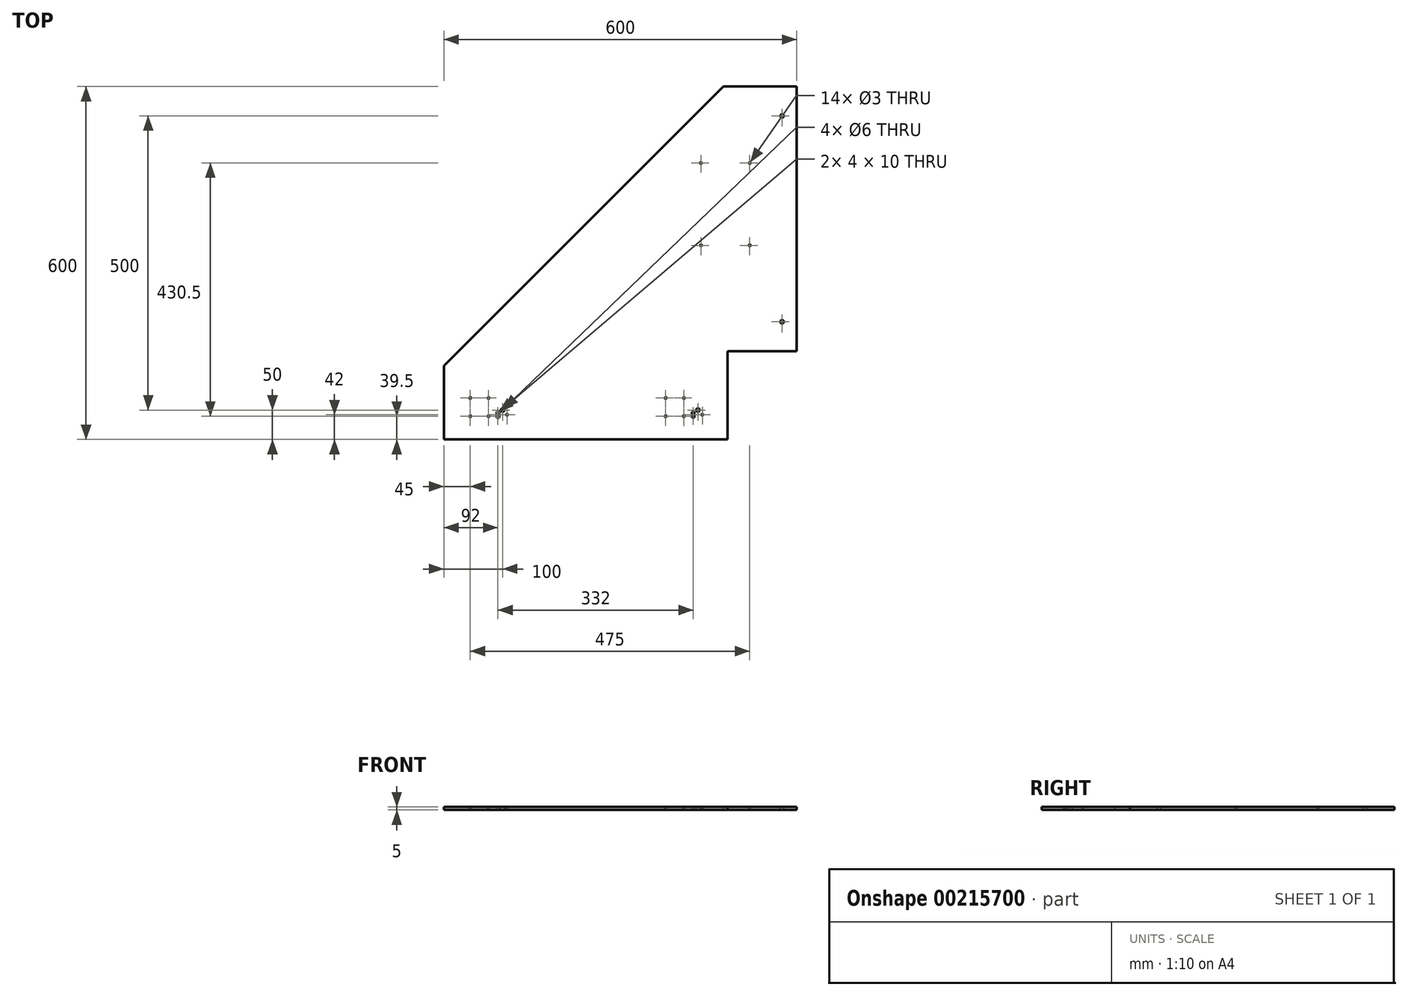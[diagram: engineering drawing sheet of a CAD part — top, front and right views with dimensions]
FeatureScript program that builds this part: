
annotation { "Feature Type Name" : "Feature", "Feature Type Description" : "" }
export const myFeature = defineFeature(function(context is Context, id is Id, definition is map)
    precondition{}
    {
        {
            var Q0;
            Q0=qCreatedBy(makeId("Top.planeOp"),FACE);
            var sketch = newSketch(context, id + "F0", { "sketchPlane" : qUnion([Q0])});
            skLineSegment(sketch, "E0.bottom", {"start": v(-300, 300) * mm, "end": v(300, 300) * mm});
            skLineSegment(sketch, "E0.top", {"start": v(-300, -300) * mm, "end": v(300, -300) * mm});
            skLineSegment(sketch, "E0.left", {"start": v(-300, 300) * mm, "end": v(-300, -300) * mm});
            skLineSegment(sketch, "E0.right", {"start": v(300, 300) * mm, "end": v(300, -300) * mm});
            skSolve(sketch);
        }
        {
            var Q0;
            Q0=makeQuery(id+"F0.imprint","IMPRINT",FACE,{"disambiguationData":[TD([[makeQuery(id+"F0.imprint","IMPRINT",EDGE,{"derivedFrom":sQuery(id+"F0.wireOp",EDGE,"E0.bottom")}),-1.0]])]});
            extrude(context, id + "F1", {"entities" : qUnion([Q0]), "depth" : 5 * mm});
        }
        {
            var Q0;
            Q0=makeQuery(id+"F1.opExtrude","CAP_FACE",FACE,{"disambiguationData":[OSD([sQuery(id+"F0.wireOp",EDGE,"E0.bottom"),sQuery(id+"F0.wireOp",EDGE,"E0.top"),sQuery(id+"F0.wireOp",EDGE,"E0.left"),sQuery(id+"F0.wireOp",EDGE,"E0.right")])],"isStart":false});
            var sketch = newSketch(context, id + "F2", { "sketchPlane" : qUnion([Q0])});
            skCircle(sketch, "E1", {"center": v(-255, -229.5) * mm, "radius": 1.5 * mm});
            skCircle(sketch, "E2.MirrorC", {"center": v(-255, -260.5) * mm, "radius": 1.5 * mm});
            skCircle(sketch, "E3.MirrorC", {"center": v(-224, -229.5) * mm, "radius": 1.5 * mm});
            skCircle(sketch, "E4.MirrorC", {"center": v(-224, -260.5) * mm, "radius": 1.5 * mm});
            skCircle(sketch, "E5", {"center": v(-200, -250) * mm, "radius": 3 * mm});
            skLineSegment(sketch, "E6.bottom", {"start": v(-210, -253) * mm, "end": v(-206, -253) * mm});
            skLineSegment(sketch, "E6.top", {"start": v(-210, -263) * mm, "end": v(-206, -263) * mm});
            skLineSegment(sketch, "E6.left", {"start": v(-210, -253) * mm, "end": v(-210, -263) * mm});
            skLineSegment(sketch, "E6.right", {"start": v(-206, -253) * mm, "end": v(-206, -263) * mm});
            skCircle(sketch, "E7", {"center": v(-192.5, -258) * mm, "radius": 1.5 * mm});
            skPoint(sketch, "E8", {"position": v(-206, -258) * mm});
            skLineSegment(sketch, "E9", {"start": v(-215, -229.5) * mm, "end": v(-215, -260.5) * mm, "construction": true});
            skLineSegment(sketch, "E10", {"start": v(-239.5, -229.5) * mm, "end": v(-239.5, -260.5) * mm, "construction": true});
            skLineSegment(sketch, "E11", {"start": v(-264, -245) * mm, "end": v(-215, -245) * mm, "construction": true});
            skCircle(sketch, "E12", {"center": v(77, -229.5) * mm, "radius": 1.5 * mm});
            skCircle(sketch, "E13.MirrorC", {"center": v(77, -260.5) * mm, "radius": 1.5 * mm});
            skCircle(sketch, "E14.MirrorC", {"center": v(108, -229.5) * mm, "radius": 1.5 * mm});
            skCircle(sketch, "E15.MirrorC", {"center": v(108, -260.5) * mm, "radius": 1.5 * mm});
            skCircle(sketch, "E16", {"center": v(132, -250) * mm, "radius": 3 * mm});
            skLineSegment(sketch, "E17.bottom", {"start": v(122, -253) * mm, "end": v(126, -253) * mm});
            skLineSegment(sketch, "E17.top", {"start": v(122, -263) * mm, "end": v(126, -263) * mm});
            skLineSegment(sketch, "E17.left", {"start": v(122, -253) * mm, "end": v(122, -263) * mm});
            skLineSegment(sketch, "E17.right", {"start": v(126, -253) * mm, "end": v(126, -263) * mm});
            skCircle(sketch, "E18", {"center": v(139.5, -258) * mm, "radius": 1.5 * mm});
            skPoint(sketch, "E19", {"position": v(126, -258) * mm});
            skLineSegment(sketch, "E20", {"start": v(117, -229.5) * mm, "end": v(117, -260.5) * mm, "construction": true});
            skLineSegment(sketch, "E21", {"start": v(92.5, -229.5) * mm, "end": v(92.5, -260.5) * mm, "construction": true});
            skLineSegment(sketch, "E22", {"start": v(68, -245) * mm, "end": v(117, -245) * mm, "construction": true});
            skLineSegment(sketch, "E23", {"start": v(182, -150) * mm, "end": v(300, -150) * mm});
            skLineSegment(sketch, "E24", {"start": v(182, -150) * mm, "end": v(182, -300) * mm});
            skLineSegment(sketch, "E25", {"start": v(275, -150) * mm, "end": v(275, 300) * mm, "construction": true});
            skCircle(sketch, "E26", {"center": v(275, -100) * mm, "radius": 3 * mm});
            skCircle(sketch, "E27", {"center": v(275, 250) * mm, "radius": 3 * mm});
            skLineSegment(sketch, "E28", {"start": v(300, -150) * mm, "end": v(300, -300) * mm});
            skLineSegment(sketch, "E29", {"start": v(300, -300) * mm, "end": v(182, -300) * mm});
            skCircle(sketch, "E30", {"center": v(220, 30) * mm, "radius": 1.5 * mm});
            skCircle(sketch, "E31", {"center": v(137, 30) * mm, "radius": 1.5 * mm});
            skCircle(sketch, "E32.MirrorC", {"center": v(137, 170) * mm, "radius": 1.5 * mm});
            skCircle(sketch, "E33.MirrorC", {"center": v(220, 170) * mm, "radius": 1.5 * mm});
            skLineSegment(sketch, "E34", {"start": v(-300, 0) * mm, "end": v(300, 0) * mm, "construction": true});
            skLineSegment(sketch, "E35", {"start": v(-300, -175) * mm, "end": v(175, 300) * mm});
            skLineSegment(sketch, "E36", {"start": v(-300, -175) * mm, "end": v(-300, 300) * mm});
            skLineSegment(sketch, "E37", {"start": v(-300, 300) * mm, "end": v(175, 300) * mm});
            skSolve(sketch);
        }
        {
            var Q0;
            Q0=qSketchRegion(id+"F2",true);
            extrude(context, id + "F3", {"entities" : qUnion([Q0]), "operationType" : NewBodyOperationType.REMOVE, "endBound" : BoundingType.THROUGH_ALL, "oppositeDirection" : true, "depth" : 25 * mm});
        }
    });
